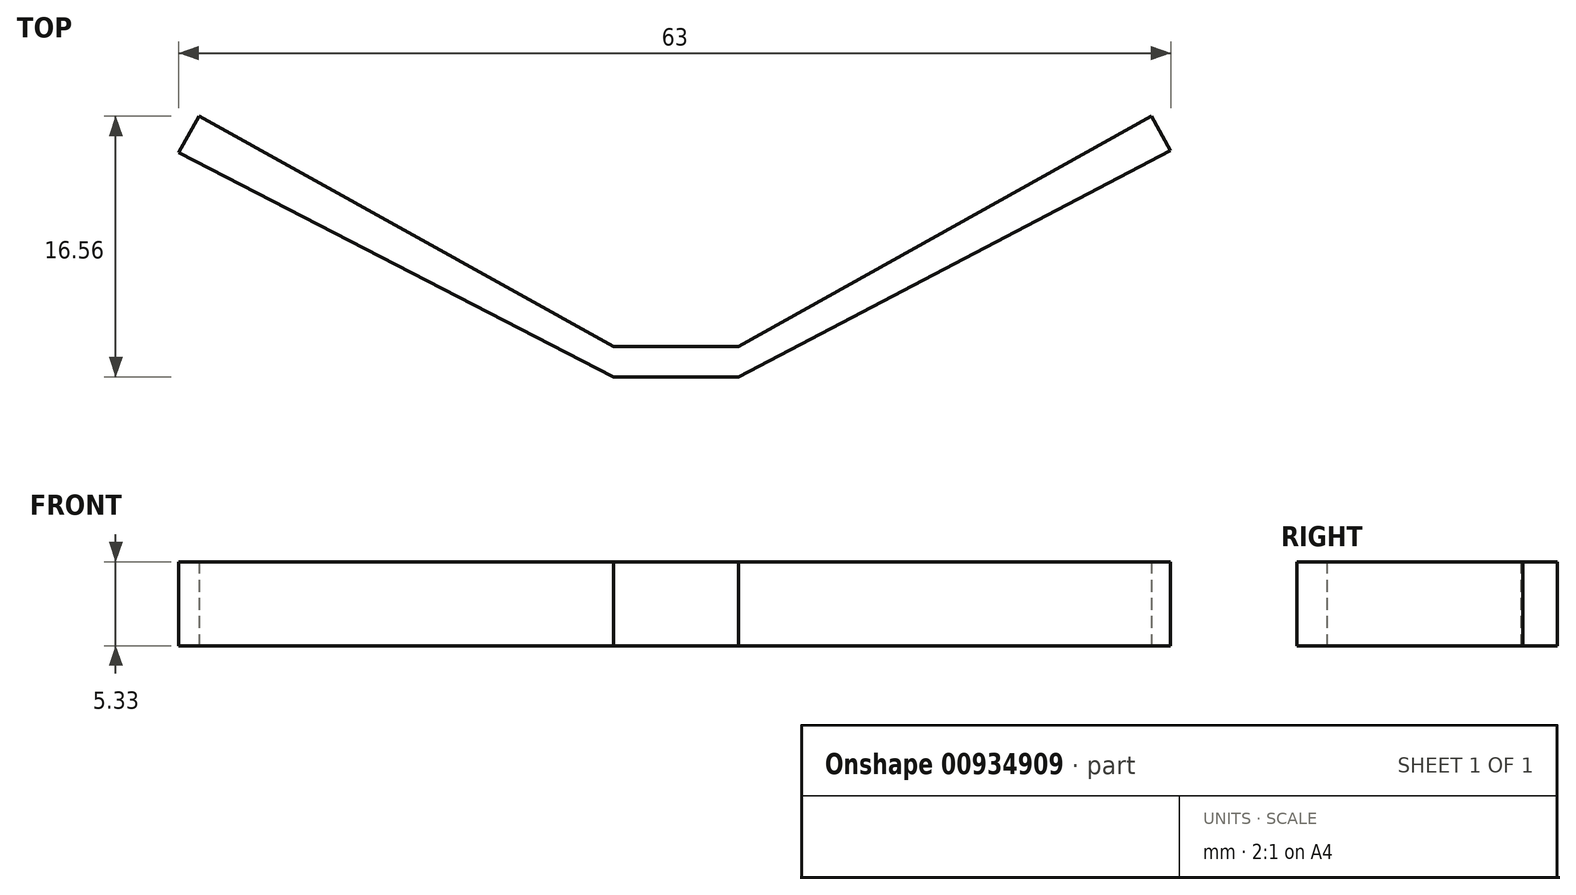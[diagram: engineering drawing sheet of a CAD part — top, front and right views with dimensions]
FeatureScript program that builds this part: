
annotation { "Feature Type Name" : "Feature", "Feature Type Description" : "" }
export const myFeature = defineFeature(function(context is Context, id is Id, definition is map)
    precondition{}
    {
        {
            var Q0;
            Q0=qCreatedBy(makeId("Top.planeOp"),FACE);
            var sketch = newSketch(context, id + "F0", { "sketchPlane" : qUnion([Q0])});
            skLineSegment(sketch, "E0.bottom", {"start": v(18.55, 0) * mm, "end": v(10.6, 0) * mm});
            skLineSegment(sketch, "E0.top", {"start": v(18.55, 1.93) * mm, "end": v(10.6, 1.93) * mm});
            skLineSegment(sketch, "E0.left", {"start": v(18.55, 0) * mm, "end": v(18.55, 1.93) * mm});
            skLineSegment(sketch, "E0.right", {"start": v(10.6, 0) * mm, "end": v(10.6, 1.93) * mm});
            skLineSegment(sketch, "E1", {"start": v(10.6, 1.93) * mm, "end": v(-15.73, 16.56) * mm});
            skLineSegment(sketch, "E2", {"start": v(-15.73, 16.56) * mm, "end": v(-17.01, 14.25) * mm});
            skLineSegment(sketch, "E3", {"start": v(-17.01, 14.25) * mm, "end": v(10.6, 0) * mm});
            skLineSegment(sketch, "E4", {"start": v(18.55, 1.93) * mm, "end": v(44.76, 16.56) * mm});
            skLineSegment(sketch, "E5", {"start": v(44.76, 16.56) * mm, "end": v(45.99, 14.36) * mm});
            skLineSegment(sketch, "E6", {"start": v(45.99, 14.36) * mm, "end": v(18.55, 0) * mm});
            skSolve(sketch);
        }
        {
            var Q0;
            Q0=makeQuery(id+"F0.imprint","IMPRINT",FACE,{"disambiguationData":[TD([[makeQuery(id+"F0.imprint","IMPRINT",EDGE,{"derivedFrom":sQuery(id+"F0.wireOp",EDGE,"E0.left")}),-1.0]])]});
            var Q1;
            Q1=makeQuery(id+"F0.imprint","IMPRINT",FACE,{"disambiguationData":[TD([[makeQuery(id+"F0.imprint","IMPRINT",EDGE,{"derivedFrom":sQuery(id+"F0.wireOp",EDGE,"E0.right")}),1.0]])]});
            var Q2;
            Q2=makeQuery(id+"F0.imprint","IMPRINT",FACE,{"disambiguationData":[TD([[makeQuery(id+"F0.imprint","IMPRINT",EDGE,{"derivedFrom":sQuery(id+"F0.wireOp",EDGE,"E0.bottom")}),-1.0]])]});
            extrude(context, id + "F1", {"entities" : qUnion([Q0, Q1, Q2]), "depth" : 5.33 * mm, "offsetDistance" : 25.4 * mm});
        }
    });
